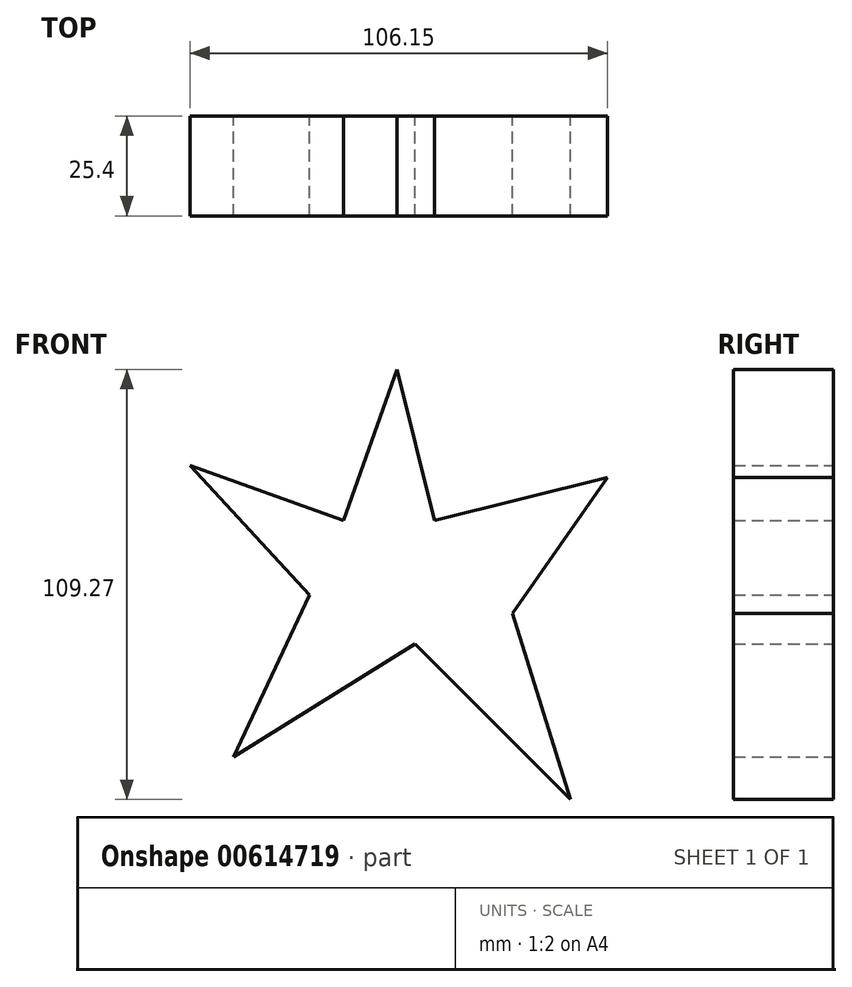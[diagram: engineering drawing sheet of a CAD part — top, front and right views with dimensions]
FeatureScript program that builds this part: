
annotation { "Feature Type Name" : "Feature", "Feature Type Description" : "" }
export const myFeature = defineFeature(function(context is Context, id is Id, definition is map)
    precondition{}
    {
        {
            var Q0;
            Q0=qCreatedBy(makeId("Front.planeOp"),FACE);
            var sketch = newSketch(context, id + "F0", { "sketchPlane" : qUnion([Q0])});
            skLineSegment(sketch, "E0", {"start": v(0, 0) * mm, "end": v(39.5, -39.5) * mm});
            skLineSegment(sketch, "E1", {"start": v(39.5, -39.5) * mm, "end": v(24.84, 7.8) * mm});
            skLineSegment(sketch, "E2", {"start": v(24.84, 7.8) * mm, "end": v(48.96, 42.34) * mm});
            skLineSegment(sketch, "E3", {"start": v(48.96, 42.34) * mm, "end": v(4.97, 31.46) * mm});
            skLineSegment(sketch, "E4", {"start": v(4.97, 31.46) * mm, "end": v(-4.5, 69.77) * mm});
            skLineSegment(sketch, "E5", {"start": v(-4.5, 69.77) * mm, "end": v(-18.21, 31.46) * mm});
            skLineSegment(sketch, "E6", {"start": v(-18.21, 31.46) * mm, "end": v(-57.2, 45.4) * mm});
            skLineSegment(sketch, "E7", {"start": v(-57.2, 45.4) * mm, "end": v(-26.73, 12.54) * mm});
            skLineSegment(sketch, "E8", {"start": v(-26.73, 12.54) * mm, "end": v(-46.12, -28.62) * mm});
            skLineSegment(sketch, "E9", {"start": v(-46.12, -28.62) * mm, "end": v(0, 0) * mm});
            skSolve(sketch);
        }
        {
            var Q0;
            Q0 = qSketchRegion(id + "F0", true);
            extrude(context, id + "F1", {"entities" : qUnion([Q0]), "endBound" : BoundingType.SYMMETRIC, "depth" : 25.4 * mm, "offsetDistance" : 25.4 * mm});
        }
    });
